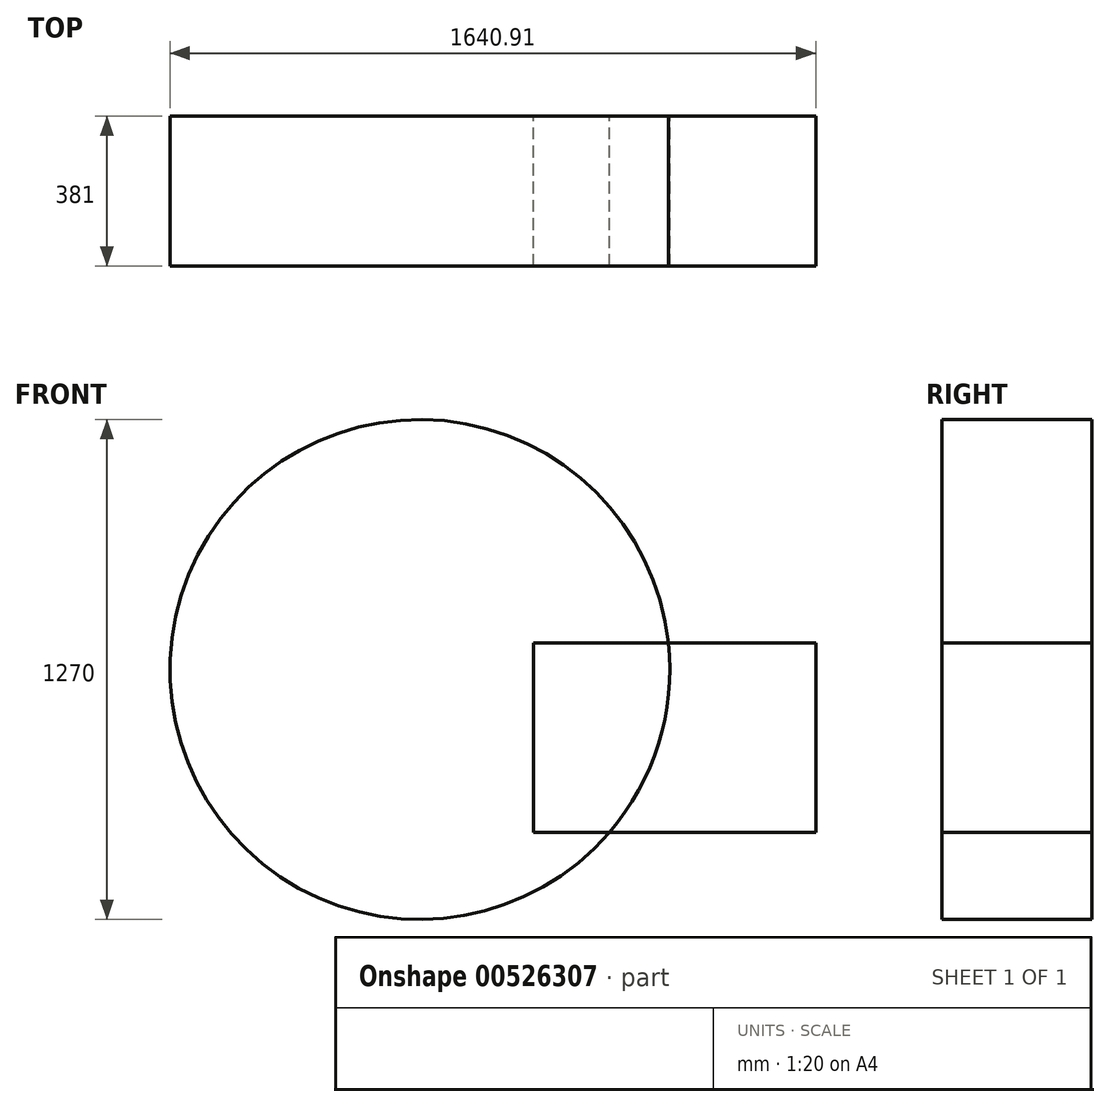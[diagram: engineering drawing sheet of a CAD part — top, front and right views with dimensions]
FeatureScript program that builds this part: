
annotation { "Feature Type Name" : "Feature", "Feature Type Description" : "" }
export const myFeature = defineFeature(function(context is Context, id is Id, definition is map)
    precondition{}
    {
        {
            var Q0;
            Q0=qCreatedBy(makeId("Front.planeOp"),FACE);
            var sketch = newSketch(context, id + "F0", { "sketchPlane" : qUnion([Q0])});
            skCircle(sketch, "E0", {"center": v(0, 0) * mm, "radius": 635 * mm});
            skLineSegment(sketch, "E1.bottom", {"start": v(289.2, 67.06) * mm, "end": v(1005.91, 67.06) * mm});
            skLineSegment(sketch, "E1.top", {"start": v(289.2, -413.51) * mm, "end": v(1005.91, -413.51) * mm});
            skLineSegment(sketch, "E1.left", {"start": v(289.2, 67.06) * mm, "end": v(289.2, -413.51) * mm});
            skLineSegment(sketch, "E1.right", {"start": v(1005.91, 67.06) * mm, "end": v(1005.91, -413.51) * mm});
            skSolve(sketch);
        }
        {
            var Q0;
            {var subQ5=sQuery(id+"F0.wireOp",EDGE,"E1.left");Q0=makeQuery(id+"F0.imprint","IMPRINT",FACE,{"disambiguationData":[TD([[makeQuery(id+"F0.imprint","IMPRINT",EDGE,{"derivedFrom":subQ5}),-1.0]])]});}
            var Q1;
            {var subQ5=sQuery(id+"F0.wireOp",EDGE,"E1.right");Q1=makeQuery(id+"F0.imprint","IMPRINT",FACE,{"disambiguationData":[TD([[makeQuery(id+"F0.imprint","IMPRINT",EDGE,{"derivedFrom":subQ5}),-1.0]])]});}
            extrude(context, id + "F1", {"entities" : qUnion([Q0, Q1]), "depth" : 381 * mm, "offsetDistance" : 25.4 * mm});
        }
    });
